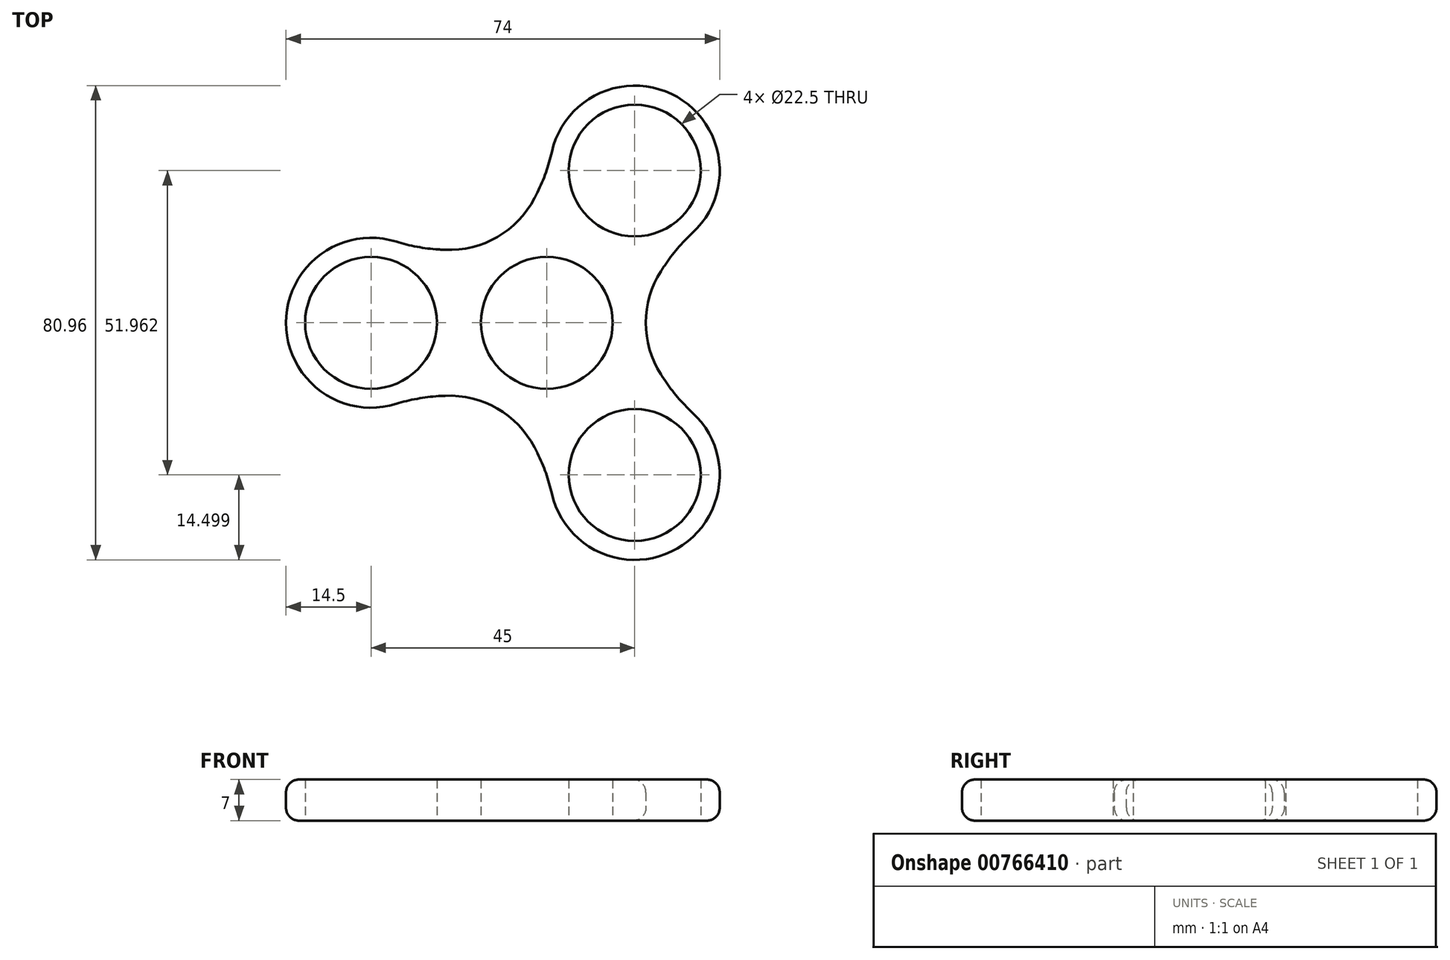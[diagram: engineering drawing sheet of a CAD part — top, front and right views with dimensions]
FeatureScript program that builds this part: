
annotation { "Feature Type Name" : "Feature", "Feature Type Description" : "" }
export const myFeature = defineFeature(function(context is Context, id is Id, definition is map)
    precondition{}
    {
        {
            var Q0;
            Q0=qCreatedBy(makeId("Top.planeOp"),FACE);
            var sketch = newSketch(context, id + "F0", { "sketchPlane" : qUnion([Q0])});
            skCircle(sketch, "E0", {"center": v(0, 0) * mm, "radius": 11.25 * mm});
            skLineSegment(sketch, "E1", {"start": v(0, 0) * mm, "end": v(-30, 0) * mm});
            skCircle(sketch, "E2", {"center": v(-30, 0) * mm, "radius": 11.25 * mm});
            skCircle(sketch, "E3", {"center": v(-30, 0) * mm, "radius": 14.5 * mm});
            skCircle(sketch, "E4", {"center": v(0, 0) * mm, "radius": 14.5 * mm});
            skArc(sketch, "E5", {"start": v(0, -14.5) * mm, "mid": v(-15, -12.4) * mm, "end": v(-30, -14.5) * mm});
            skArc(sketch, "E6.MirrorCS", {"start": v(0, 14.5) * mm, "mid": v(-15, 12.4) * mm, "end": v(-30, 14.5) * mm});
            skSolve(sketch);
        }
        {
            var Q0;
            Q0 = qSketchRegion(id + "F0", true);
            extrude(context, id + "F1", {"entities" : qUnion([Q0]), "depth" : 7 * mm, "offsetDistance" : 25 * mm});
        }
        {
            var Q0;
            Q0=makeQuery(id+"F1.opExtrude","SWEPT_BODY",BODY,{"disambiguationData":[OSD([sQuery(id+"F0.wireOp",EDGE,"E0"),sQuery(id+"F0.wireOp",EDGE,"E2"),sQuery(id+"F0.wireOp",EDGE,"E3"),sQuery(id+"F0.wireOp",EDGE,"E4"),sQuery(id+"F0.wireOp",EDGE,"E5"),sQuery(id+"F0.wireOp",EDGE,"E6.MirrorCS")])]});
            var Q1;
            Q1=makeQuery(id+"F1.opExtrude","SWEPT_FACE",FACE,{"disambiguationData":[OSD([sQuery(id+"F0.wireOp",EDGE,"E4")])]});
            circularPattern(context, id + "F2", {"entities" : qUnion([Q0]), "axis" : qUnion([Q1]), "angle" : 360 * degree, "instanceCount" : 3, "equalSpace" : true});
        }
        {
            var Q0;
            Q0=makeQuery(id+"F1.opExtrude","SWEPT_BODY",BODY,{"disambiguationData":[OSD([sQuery(id+"F0.wireOp",EDGE,"E0"),sQuery(id+"F0.wireOp",EDGE,"E2"),sQuery(id+"F0.wireOp",EDGE,"E3"),sQuery(id+"F0.wireOp",EDGE,"E4"),sQuery(id+"F0.wireOp",EDGE,"E5"),sQuery(id+"F0.wireOp",EDGE,"E6.MirrorCS")])]});
            var Q1;
            Q1=makeQuery(id+"F2.opPattern","COPY",BODY,{"derivedFrom":makeQuery(id+"F1.opExtrude","SWEPT_BODY",BODY,{"disambiguationData":[OSD([sQuery(id+"F0.wireOp",EDGE,"E0"),sQuery(id+"F0.wireOp",EDGE,"E2"),sQuery(id+"F0.wireOp",EDGE,"E3"),sQuery(id+"F0.wireOp",EDGE,"E4"),sQuery(id+"F0.wireOp",EDGE,"E5"),sQuery(id+"F0.wireOp",EDGE,"E6.MirrorCS")])]}),"instanceName":"1"});
            var Q2;
            Q2=makeQuery(id+"F2.opPattern","COPY",BODY,{"derivedFrom":makeQuery(id+"F1.opExtrude","SWEPT_BODY",BODY,{"disambiguationData":[OSD([sQuery(id+"F0.wireOp",EDGE,"E0"),sQuery(id+"F0.wireOp",EDGE,"E2"),sQuery(id+"F0.wireOp",EDGE,"E3"),sQuery(id+"F0.wireOp",EDGE,"E4"),sQuery(id+"F0.wireOp",EDGE,"E5"),sQuery(id+"F0.wireOp",EDGE,"E6.MirrorCS")])]}),"instanceName":"2"});
            booleanBodies(context, id + "F3", {"operationType" : BooleanOperationType.UNION, "tools" : qUnion([Q0, Q1, Q2])});
        }
        {
            var Q0;
            Q0=makeQuery(id+"F3.opBoolean","INTERSECT",EDGE,{"derivedFrom":[makeQuery(id+"F2.opPattern","COPY",FACE,{"derivedFrom":makeQuery(id+"F1.opExtrude","SWEPT_FACE",FACE,{"disambiguationData":[OSD([sQuery(id+"F0.wireOp",EDGE,"E6.MirrorCS")])]}),"instanceName":"1"}),makeQuery(id+"F2.opPattern","COPY",FACE,{"derivedFrom":makeQuery(id+"F1.opExtrude","SWEPT_FACE",FACE,{"disambiguationData":[OSD([sQuery(id+"F0.wireOp",EDGE,"E5")])]}),"instanceName":"2"})]});
            var Q1;
            Q1=makeQuery(id+"F3.opBoolean","INTERSECT",EDGE,{"derivedFrom":[makeQuery(id+"F1.opExtrude","SWEPT_FACE",FACE,{"disambiguationData":[OSD([sQuery(id+"F0.wireOp",EDGE,"E6.MirrorCS")])]}),makeQuery(id+"F2.opPattern","COPY",FACE,{"derivedFrom":makeQuery(id+"F1.opExtrude","SWEPT_FACE",FACE,{"disambiguationData":[OSD([sQuery(id+"F0.wireOp",EDGE,"E5")])]}),"instanceName":"1"})]});
            var Q2;
            Q2=makeQuery(id+"F3.opBoolean","INTERSECT",EDGE,{"derivedFrom":[makeQuery(id+"F1.opExtrude","SWEPT_FACE",FACE,{"disambiguationData":[OSD([sQuery(id+"F0.wireOp",EDGE,"E5")])]}),makeQuery(id+"F2.opPattern","COPY",FACE,{"derivedFrom":makeQuery(id+"F1.opExtrude","SWEPT_FACE",FACE,{"disambiguationData":[OSD([sQuery(id+"F0.wireOp",EDGE,"E6.MirrorCS")])]}),"instanceName":"2"})]});
            fillet(context, id + "F4", {"entities" : qUnion([Q0, Q1, Q2]), "radius" : 16.4 * mm, "tangentPropagation" : true, "allowEdgeOverflow" : false});
        }
        {
            var Q0;
            Q0=makeQuery(id+"F1.opExtrude","SWEPT_EDGE",EDGE,{"disambiguationData":[OSD([sQuery(id+"F0.wireOp",EDGE,"E3"),sQuery(id+"F0.wireOp",EDGE,"E6.MirrorCS")])]});
            var Q1;
            Q1=makeQuery(id+"F2.opPattern","COPY",EDGE,{"derivedFrom":makeQuery(id+"F1.opExtrude","SWEPT_EDGE",EDGE,{"disambiguationData":[OSD([sQuery(id+"F0.wireOp",EDGE,"E3"),sQuery(id+"F0.wireOp",EDGE,"E5")])]}),"instanceName":"1"});
            var Q2;
            Q2=makeQuery(id+"F2.opPattern","COPY",EDGE,{"derivedFrom":makeQuery(id+"F1.opExtrude","SWEPT_EDGE",EDGE,{"disambiguationData":[OSD([sQuery(id+"F0.wireOp",EDGE,"E3"),sQuery(id+"F0.wireOp",EDGE,"E6.MirrorCS")])]}),"instanceName":"1"});
            var Q3;
            Q3=makeQuery(id+"F2.opPattern","COPY",EDGE,{"derivedFrom":makeQuery(id+"F1.opExtrude","SWEPT_EDGE",EDGE,{"disambiguationData":[OSD([sQuery(id+"F0.wireOp",EDGE,"E3"),sQuery(id+"F0.wireOp",EDGE,"E5")])]}),"instanceName":"2"});
            var Q4;
            Q4=makeQuery(id+"F1.opExtrude","SWEPT_EDGE",EDGE,{"disambiguationData":[OSD([sQuery(id+"F0.wireOp",EDGE,"E3"),sQuery(id+"F0.wireOp",EDGE,"E5")])]});
            var Q5;
            Q5=makeQuery(id+"F2.opPattern","COPY",EDGE,{"derivedFrom":makeQuery(id+"F1.opExtrude","SWEPT_EDGE",EDGE,{"disambiguationData":[OSD([sQuery(id+"F0.wireOp",EDGE,"E3"),sQuery(id+"F0.wireOp",EDGE,"E6.MirrorCS")])]}),"instanceName":"2"});
            fillet(context, id + "F5", {"entities" : qUnion([Q0, Q1, Q2, Q3, Q4, Q5]), "radius" : 30.91 * mm, "tangentPropagation" : true, "allowEdgeOverflow" : false});
        }
        {
            var Q0;
            Q0=makeQuery(id+"F2.opPattern","COPY",EDGE,{"derivedFrom":makeQuery(id+"F1.opExtrude","CAP_EDGE",EDGE,{"disambiguationData":[OSD([sQuery(id+"F0.wireOp",EDGE,"E3")])],"isStart":false}),"instanceName":"2"});
            var Q1;
            {var subQ0=sQuery(id+"F0.wireOp",EDGE,"E6.MirrorCS");var subQ1=sQuery(id+"F0.wireOp",EDGE,"E5");var subQ2=makeQuery(id+"F1.opExtrude","CAP_FACE",FACE,{"disambiguationData":[OSD([sQuery(id+"F0.wireOp",EDGE,"E0"),sQuery(id+"F0.wireOp",EDGE,"E2"),sQuery(id+"F0.wireOp",EDGE,"E3"),sQuery(id+"F0.wireOp",EDGE,"E4"),subQ1,subQ0])],"isStart":true});Q1=makeQuery(id+"F4.opFillet","BLEND_EDGE",EDGE,{"blendedFrom":[makeQuery(id+"F3.opBoolean","INTERSECT",EDGE,{"derivedFrom":[makeQuery(id+"F1.opExtrude","SWEPT_FACE",FACE,{"disambiguationData":[OSD([subQ1])]}),makeQuery(id+"F2.opPattern","COPY",FACE,{"derivedFrom":makeQuery(id+"F1.opExtrude","SWEPT_FACE",FACE,{"disambiguationData":[OSD([subQ0])]}),"instanceName":"2"})]}),makeQuery(id+"F3.opBoolean","MERGE",FACE,{"derivedFrom":[subQ2,makeQuery(id+"F2.opPattern","COPY",FACE,{"derivedFrom":subQ2,"instanceName":"1"}),makeQuery(id+"F2.opPattern","COPY",FACE,{"derivedFrom":subQ2,"instanceName":"2"})]})],"blendedInto":[makeQuery(id+"F3.opBoolean","MERGE",FACE,{"derivedFrom":[subQ2,makeQuery(id+"F2.opPattern","COPY",FACE,{"derivedFrom":subQ2,"instanceName":"1"}),makeQuery(id+"F2.opPattern","COPY",FACE,{"derivedFrom":subQ2,"instanceName":"2"})]})]});}
            var Q2;
            Q2=makeQuery(id+"F2.opPattern","COPY",EDGE,{"derivedFrom":makeQuery(id+"F1.opExtrude","CAP_EDGE",EDGE,{"disambiguationData":[OSD([sQuery(id+"F0.wireOp",EDGE,"E6.MirrorCS")])],"isStart":true}),"instanceName":"2"});
            fillet(context, id + "F6", {"entities" : qUnion([Q0, Q1, Q2]), "radius" : 2.17 * mm, "tangentPropagation" : true, "allowEdgeOverflow" : false});
        }
    });
